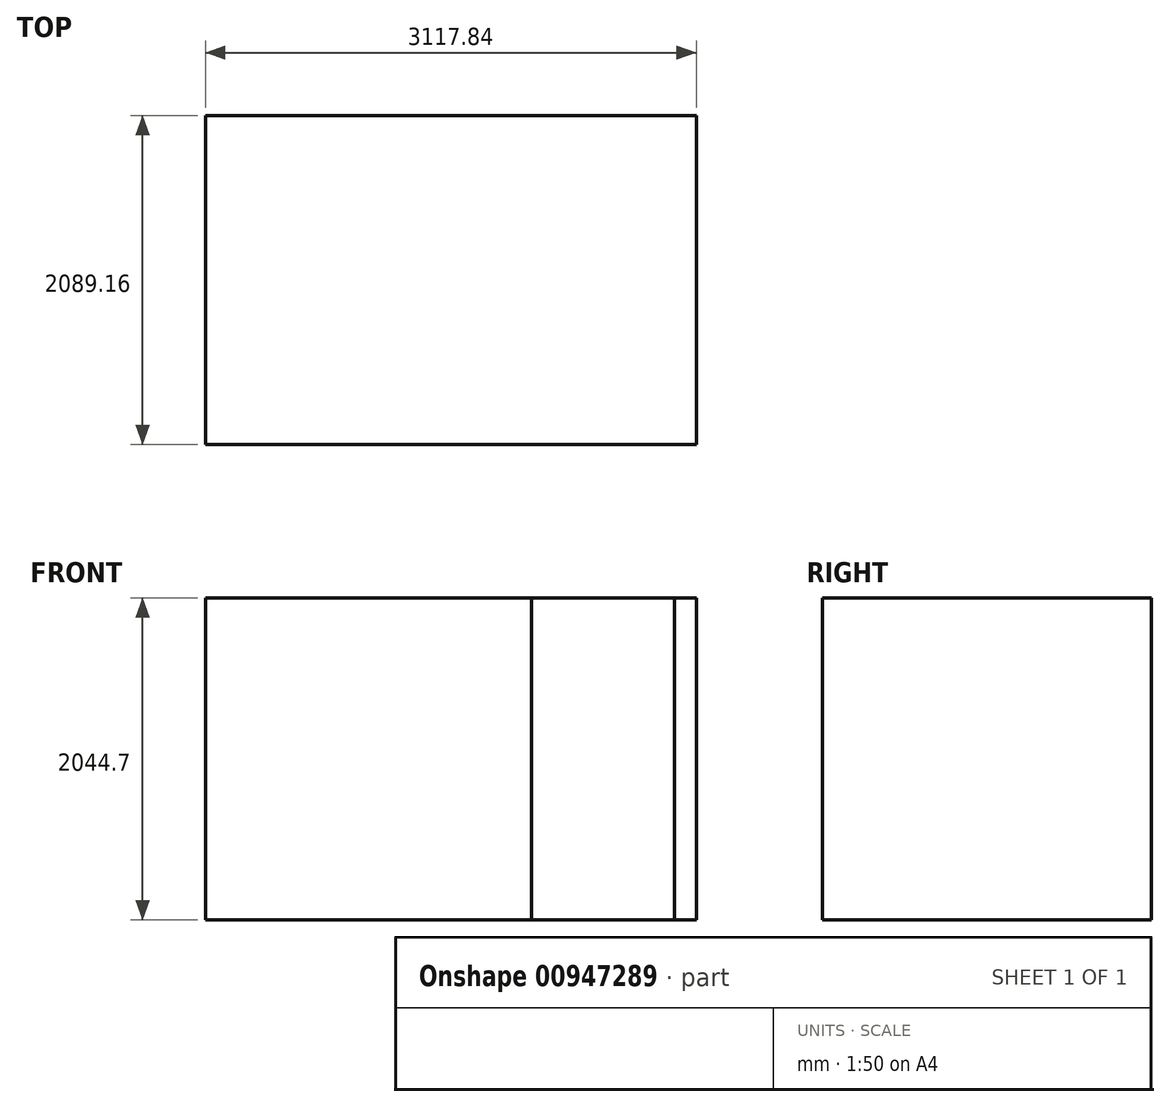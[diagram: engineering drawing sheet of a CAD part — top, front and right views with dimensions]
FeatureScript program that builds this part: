
annotation { "Feature Type Name" : "Feature", "Feature Type Description" : "" }
export const myFeature = defineFeature(function(context is Context, id is Id, definition is map)
    precondition{}
    {
        {
            var Q0;
            Q0=qCreatedBy(makeId("Front.planeOp"),FACE);
            var sketch = newSketch(context, id + "F0", { "sketchPlane" : qUnion([Q0])});
            skLineSegment(sketch, "E0.bottom", {"start": v(-1558.92, 1022.35) * mm, "end": v(1558.93, 1022.35) * mm});
            skLineSegment(sketch, "E0.top", {"start": v(-1558.93, -1022.35) * mm, "end": v(1558.92, -1022.35) * mm});
            skLineSegment(sketch, "E0.left", {"start": v(-1558.92, 1022.35) * mm, "end": v(-1558.93, -1022.35) * mm});
            skLineSegment(sketch, "E0.right", {"start": v(1558.93, 1022.35) * mm, "end": v(1558.92, -1022.35) * mm});
            skPoint(sketch, "E0.middle", {"position": v(0, 0) * mm});
            skSolve(sketch);
        }
        {
            var Q0;
            Q0=sQuery(id+"F0.wireOp",EDGE,"E0.left");
            var Q1;
            Q1=sQuery(id+"F0.wireOp",EDGE,"E0.top");
            var Q2;
            Q2=sQuery(id+"F0.wireOp",EDGE,"E0.right");
            extrude(context, id + "F1", {"bodyType" : ToolBodyType.SURFACE, "surfaceEntities" : qUnion([Q0, Q1, Q2]), "endBound" : BoundingType.SYMMETRIC, "depth" : 2089.15 * mm, "offsetDistance" : 25.4 * mm});
        }
        {
            var Q0;
            Q0=makeQuery(id+"F1.opExtrude","SWEPT_FACE",FACE,{"disambiguationData":[OSD([sQuery(id+"F0.wireOp",EDGE,"E0.top")])]});
            var sketch = newSketch(context, id + "F2", { "sketchPlane" : qUnion([Q0])});
            skLineSegment(sketch, "E1", {"start": v(-1558.93, -1044.58) * mm, "end": v(1558.92, -1044.58) * mm});
            skLineSegment(sketch, "E2", {"start": v(-1558.93, 1044.58) * mm, "end": v(511.17, 1044.58) * mm});
            skLineSegment(sketch, "E3", {"start": v(1419.22, 1044.58) * mm, "end": v(1558.92, 1044.58) * mm});
            skSolve(sketch);
        }
        {
            var Q0;
            Q0=sQuery(id+"F2.wireOp",EDGE,"E1");
            var Q1;
            Q1=sQuery(id+"F2.wireOp",EDGE,"E2");
            var Q2;
            Q2=sQuery(id+"F2.wireOp",EDGE,"E3");
            extrude(context, id + "F3", {"bodyType" : ToolBodyType.SURFACE, "surfaceOperationType" : NewSurfaceOperationType.ADD, "surfaceEntities" : qUnion([Q0, Q1, Q2]), "oppositeDirection" : true, "depth" : 2044.7 * mm, "offsetDistance" : 25.4 * mm});
        }
    });
